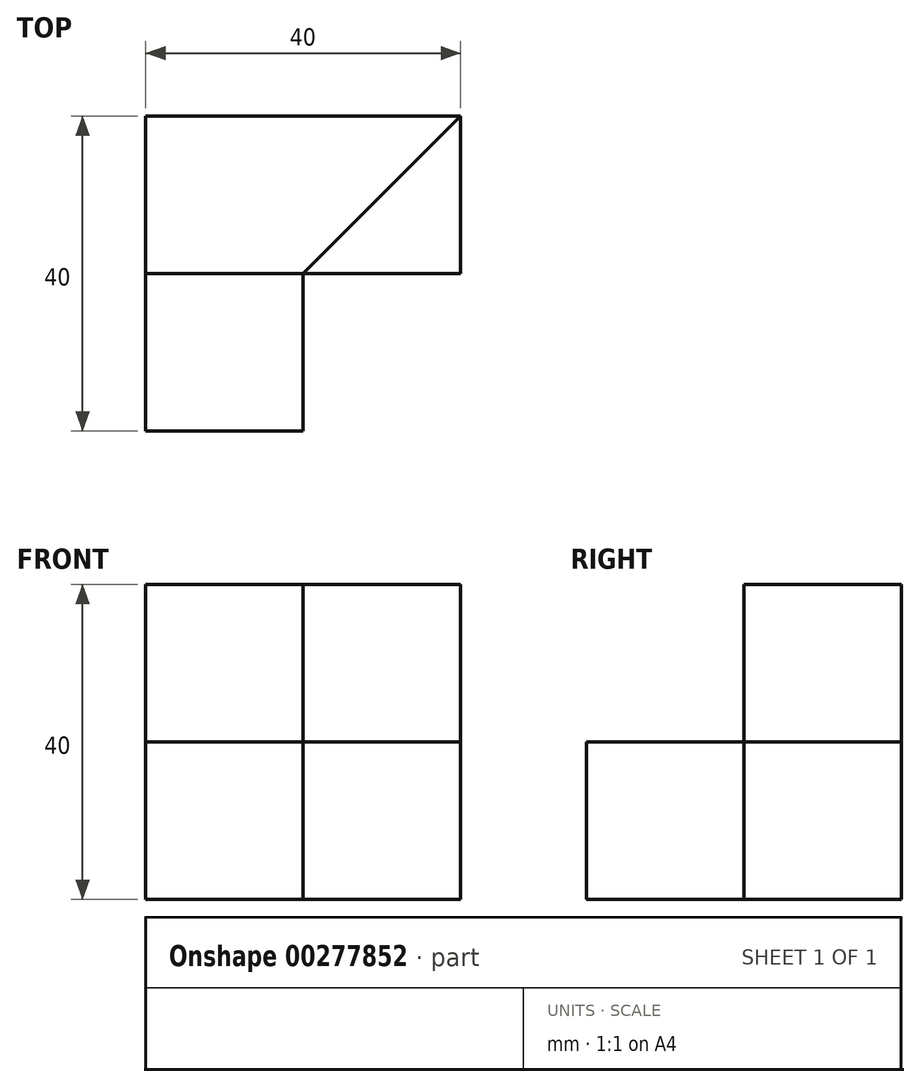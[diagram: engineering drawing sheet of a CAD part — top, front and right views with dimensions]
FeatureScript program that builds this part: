
annotation { "Feature Type Name" : "Feature", "Feature Type Description" : "" }
export const myFeature = defineFeature(function(context is Context, id is Id, definition is map)
    precondition{}
    {
        {
            var Q0;
            Q0=qCreatedBy(makeId("Top.planeOp"),FACE);
            var sketch = newSketch(context, id + "F0", { "sketchPlane" : qUnion([Q0])});
            skLineSegment(sketch, "E0.bottom", {"start": v(0, 0) * mm, "end": v(20, 0) * mm});
            skLineSegment(sketch, "E0.top", {"start": v(0, 40) * mm, "end": v(40, 40) * mm});
            skLineSegment(sketch, "E0.left", {"start": v(0, 0) * mm, "end": v(0, 40) * mm});
            skLineSegment(sketch, "E0.right", {"start": v(40, 20) * mm, "end": v(40, 40) * mm});
            skLineSegment(sketch, "E1", {"start": v(20, 0) * mm, "end": v(20, 20) * mm});
            skPoint(sketch, "E1.endSnap0", {"position": v(40, 20) * mm});
            skLineSegment(sketch, "E2", {"start": v(20, 20) * mm, "end": v(40, 20) * mm});
            skPoint(sketch, "E3.orphan", {"position": v(40, 0) * mm});
            skSolve(sketch);
        }
        {
            var Q0;
            Q0 = qSketchRegion(id + "F0", true);
            extrude(context, id + "F1", {"entities" : qUnion([Q0]), "depth" : 20 * mm});
        }
        {
            var Q0;
            Q0=makeQuery(id+"F1.opExtrude","CAP_FACE",FACE,{"disambiguationData":[OSD([sQuery(id+"F0.wireOp",EDGE,"E0.bottom"),sQuery(id+"F0.wireOp",EDGE,"E0.top"),sQuery(id+"F0.wireOp",EDGE,"E0.left"),sQuery(id+"F0.wireOp",EDGE,"E0.right"),sQuery(id+"F0.wireOp",EDGE,"E1"),sQuery(id+"F0.wireOp",EDGE,"E2")])],"isStart":false});
            var sketch = newSketch(context, id + "F2", { "sketchPlane" : qUnion([Q0])});
            skLineSegment(sketch, "E4", {"start": v(20, 20) * mm, "end": v(0, 20) * mm});
            skLineSegment(sketch, "E5", {"start": v(20, 20) * mm, "end": v(40, 40) * mm});
            skLineSegment(sketch, "E6.0", {"start": v(0, 40) * mm, "end": v(40, 40) * mm});
            skLineSegment(sketch, "E7.0", {"start": v(0, 20) * mm, "end": v(0, 40) * mm});
            skPoint(sketch, "E8.orphan", {"position": v(0, 0) * mm});
            skSolve(sketch);
        }
        {
            var Q0;
            Q0 = qSketchRegion(id + "F2", true);
            extrude(context, id + "F3", {"entities" : qUnion([Q0]), "operationType" : NewBodyOperationType.ADD, "depth" : 20 * mm});
        }
    });
